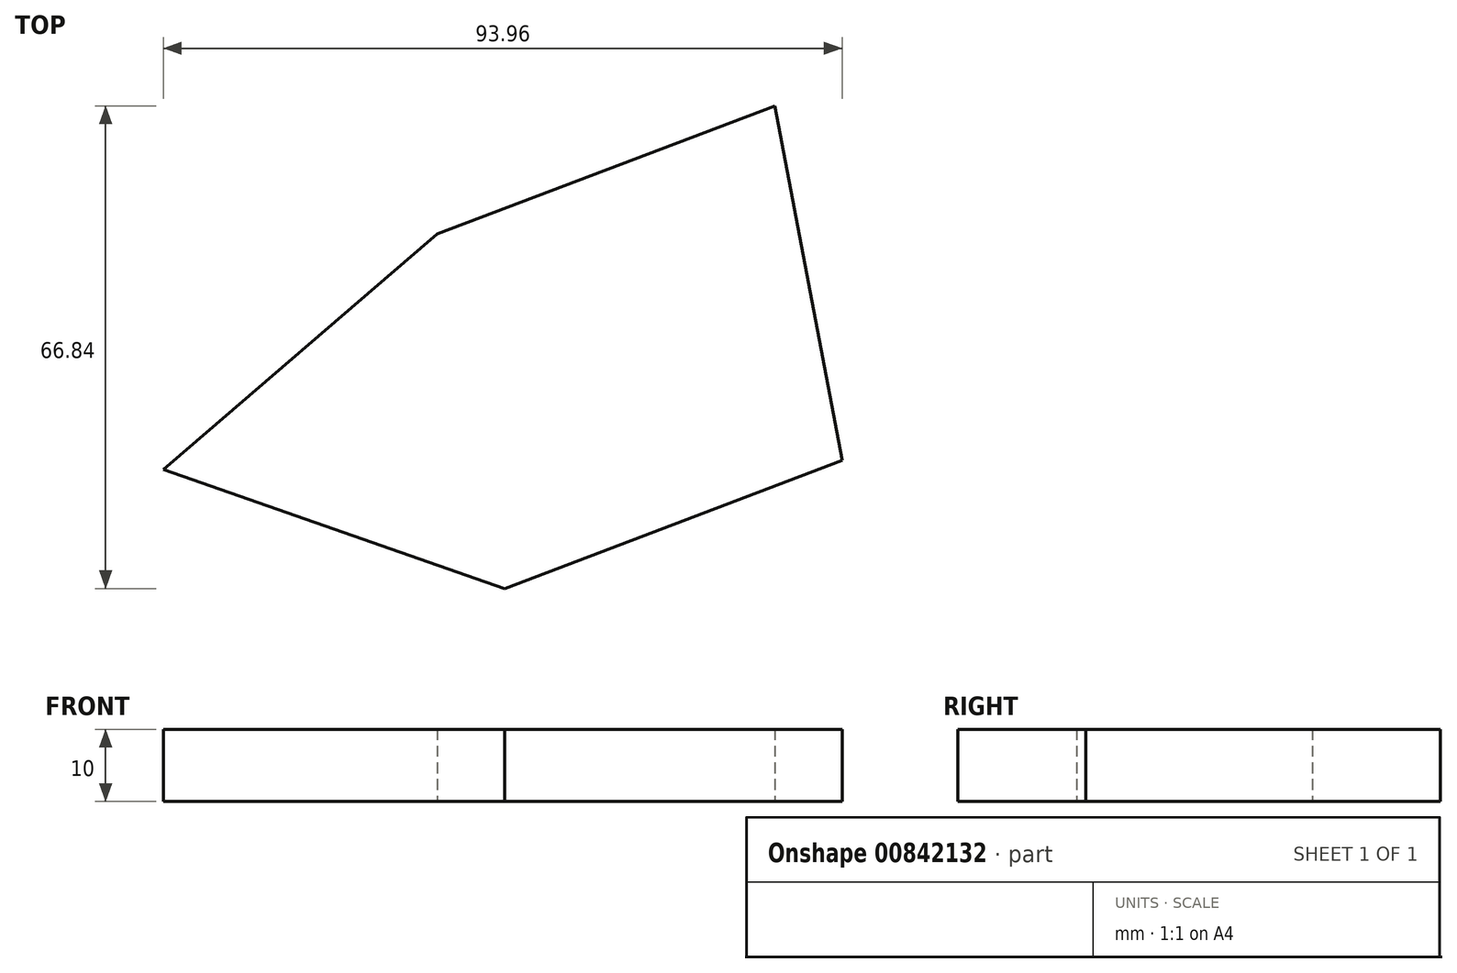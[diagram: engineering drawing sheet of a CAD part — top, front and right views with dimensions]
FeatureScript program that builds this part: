
annotation { "Feature Type Name" : "Feature", "Feature Type Description" : "" }
export const myFeature = defineFeature(function(context is Context, id is Id, definition is map)
    precondition{}
    {
        {
            var Q0;
            Q0=qCreatedBy(makeId("Top.planeOp"),FACE);
            var sketch = newSketch(context, id + "F0", { "sketchPlane" : qUnion([Q0])});
            skLineSegment(sketch, "E0", {"start": v(0, 0) * mm, "end": v(37.87, 32.64) * mm});
            skLineSegment(sketch, "E1", {"start": v(37.87, 32.64) * mm, "end": v(84.63, 50.36) * mm});
            skLineSegment(sketch, "E2", {"start": v(84.63, 50.36) * mm, "end": v(93.96, 1.24) * mm});
            skLineSegment(sketch, "E3", {"start": v(93.96, 1.24) * mm, "end": v(47.2, -16.48) * mm});
            skLineSegment(sketch, "E4", {"start": v(47.2, -16.48) * mm, "end": v(0, 0) * mm});
            skSolve(sketch);
        }
        {
            var Q0;
            Q0=makeQuery(id+"F0.imprint","IMPRINT",FACE,{"disambiguationData":[TD([[makeQuery(id+"F0.imprint","IMPRINT",EDGE,{"derivedFrom":sQuery(id+"F0.wireOp",EDGE,"E0")}),-1.0]])]});
            extrude(context, id + "F1", {"entities" : qUnion([Q0]), "depth" : 10 * mm, "offsetDistance" : 25 * mm});
        }
    });
